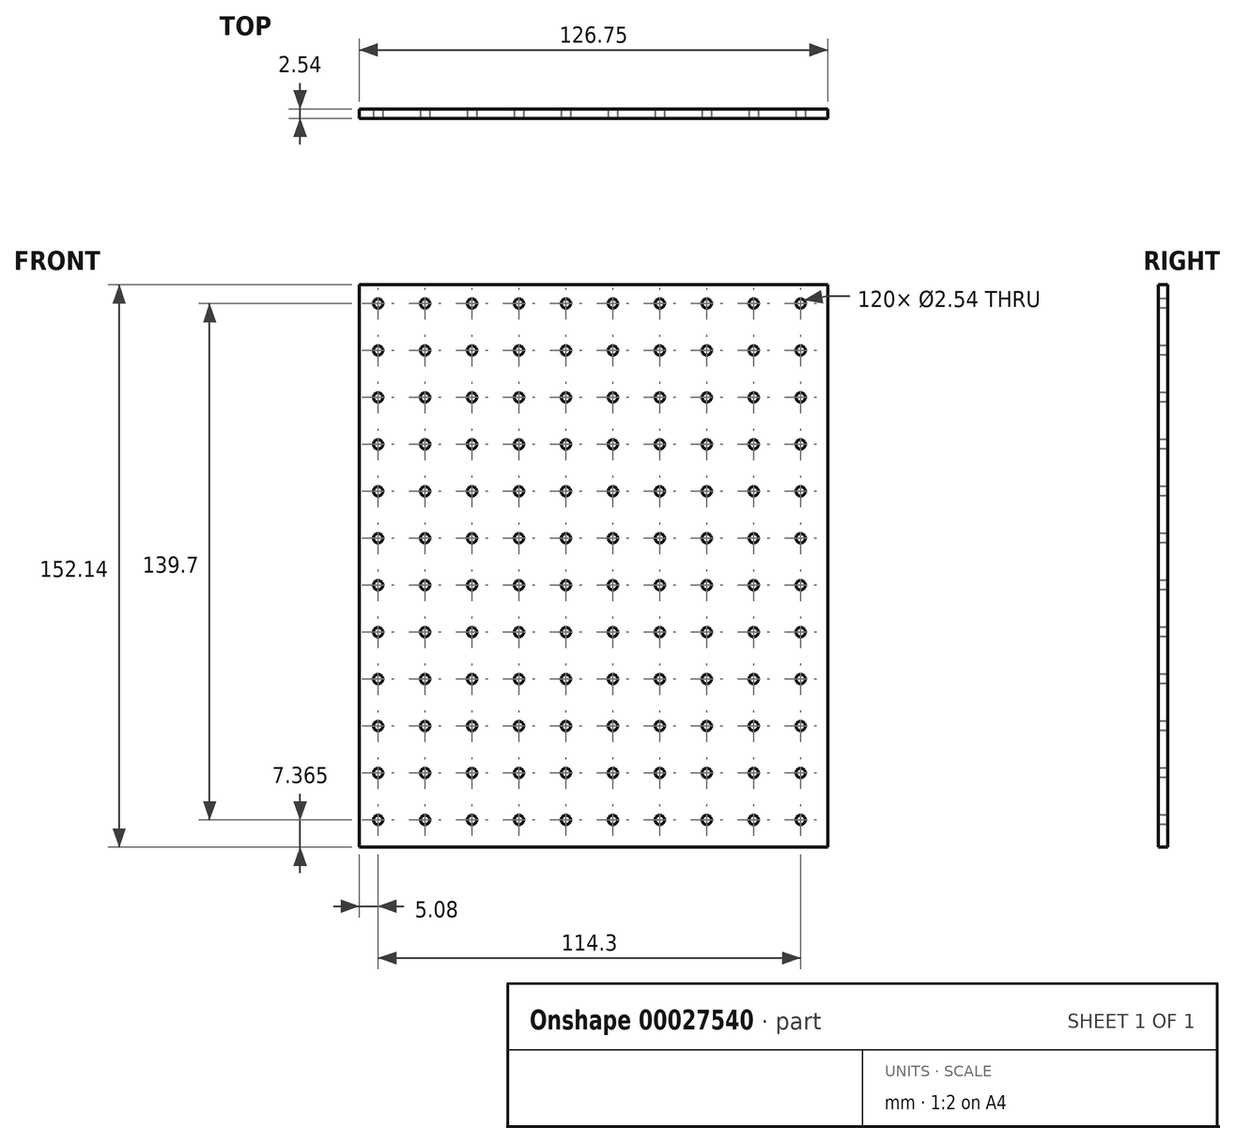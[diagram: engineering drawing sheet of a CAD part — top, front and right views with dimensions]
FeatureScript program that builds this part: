
annotation { "Feature Type Name" : "Feature", "Feature Type Description" : "" }
export const myFeature = defineFeature(function(context is Context, id is Id, definition is map)
    precondition{}
    {
        {
            var Q0;
            Q0=qCreatedBy(makeId("Front.planeOp"),FACE);
            var sketch = newSketch(context, id + "F0", { "sketchPlane" : qUnion([Q0])});
            skLineSegment(sketch, "E0.bottom", {"start": v(-42.7, 126.61) * mm, "end": v(84.04, 126.61) * mm});
            skLineSegment(sketch, "E0.top", {"start": v(-42.7, -25.53) * mm, "end": v(84.04, -25.53) * mm});
            skLineSegment(sketch, "E0.left", {"start": v(-42.7, 126.61) * mm, "end": v(-42.7, -25.53) * mm});
            skLineSegment(sketch, "E0.right", {"start": v(84.04, 126.61) * mm, "end": v(84.04, -25.53) * mm});
            skSolve(sketch);
        }
        {
            var Q0;
            Q0=makeQuery(id+"F0.imprint","IMPRINT",FACE,{"disambiguationData":[TD([[makeQuery(id+"F0.imprint","IMPRINT",EDGE,{"derivedFrom":sQuery(id+"F0.wireOp",EDGE,"E0.bottom")}),-1.0]])]});
            extrude(context, id + "F1", {"entities" : qUnion([Q0]), "depth" : 2.54 * mm});
        }
        {
            var Q0;
            Q0=makeQuery(id+"F1.opExtrude","CAP_FACE",FACE,{"disambiguationData":[OSD([sQuery(id+"F0.wireOp",EDGE,"E0.bottom"),sQuery(id+"F0.wireOp",EDGE,"E0.top"),sQuery(id+"F0.wireOp",EDGE,"E0.left"),sQuery(id+"F0.wireOp",EDGE,"E0.right")])],"isStart":false});
            var sketch = newSketch(context, id + "F2", { "sketchPlane" : qUnion([Q0])});
            skCircle(sketch, "E1", {"center": v(-37.63, 121.53) * mm, "radius": 1.27 * mm});
            skCircle(sketch, "E2.0.1.0", {"center": v(-37.63, 108.83) * mm, "radius": 1.27 * mm});
            skCircle(sketch, "E2.0.2.0", {"center": v(-37.63, 96.13) * mm, "radius": 1.27 * mm});
            skCircle(sketch, "E2.0.3.0", {"center": v(-37.63, 83.43) * mm, "radius": 1.27 * mm});
            skCircle(sketch, "E2.0.4.0", {"center": v(-37.63, 70.73) * mm, "radius": 1.27 * mm});
            skCircle(sketch, "E2.0.5.0", {"center": v(-37.63, 58.03) * mm, "radius": 1.27 * mm});
            skCircle(sketch, "E2.0.6.0", {"center": v(-37.63, 45.33) * mm, "radius": 1.27 * mm});
            skCircle(sketch, "E2.0.7.0", {"center": v(-37.63, 32.63) * mm, "radius": 1.27 * mm});
            skCircle(sketch, "E2.0.8.0", {"center": v(-37.63, 19.93) * mm, "radius": 1.27 * mm});
            skCircle(sketch, "E2.0.9.0", {"center": v(-37.63, 7.23) * mm, "radius": 1.27 * mm});
            skCircle(sketch, "E2.0.10.0", {"center": v(-37.63, -5.47) * mm, "radius": 1.27 * mm});
            skCircle(sketch, "E2.0.11.0", {"center": v(-37.63, -18.17) * mm, "radius": 1.27 * mm});
            skCircle(sketch, "E2.1.0.0", {"center": v(-24.93, 121.53) * mm, "radius": 1.27 * mm});
            skCircle(sketch, "E2.1.1.0", {"center": v(-24.93, 108.83) * mm, "radius": 1.27 * mm});
            skCircle(sketch, "E2.1.2.0", {"center": v(-24.93, 96.13) * mm, "radius": 1.27 * mm});
            skCircle(sketch, "E2.1.3.0", {"center": v(-24.93, 83.43) * mm, "radius": 1.27 * mm});
            skCircle(sketch, "E2.1.4.0", {"center": v(-24.93, 70.73) * mm, "radius": 1.27 * mm});
            skCircle(sketch, "E2.1.5.0", {"center": v(-24.93, 58.03) * mm, "radius": 1.27 * mm});
            skCircle(sketch, "E2.1.6.0", {"center": v(-24.93, 45.33) * mm, "radius": 1.27 * mm});
            skCircle(sketch, "E2.1.7.0", {"center": v(-24.93, 32.63) * mm, "radius": 1.27 * mm});
            skCircle(sketch, "E2.1.8.0", {"center": v(-24.93, 19.93) * mm, "radius": 1.27 * mm});
            skCircle(sketch, "E2.1.9.0", {"center": v(-24.93, 7.23) * mm, "radius": 1.27 * mm});
            skCircle(sketch, "E2.1.10.0", {"center": v(-24.93, -5.47) * mm, "radius": 1.27 * mm});
            skCircle(sketch, "E2.1.11.0", {"center": v(-24.93, -18.17) * mm, "radius": 1.27 * mm});
            skCircle(sketch, "E2.2.0.0", {"center": v(-12.23, 121.53) * mm, "radius": 1.27 * mm});
            skCircle(sketch, "E2.2.1.0", {"center": v(-12.23, 108.83) * mm, "radius": 1.27 * mm});
            skCircle(sketch, "E2.2.2.0", {"center": v(-12.23, 96.13) * mm, "radius": 1.27 * mm});
            skCircle(sketch, "E2.2.3.0", {"center": v(-12.23, 83.43) * mm, "radius": 1.27 * mm});
            skCircle(sketch, "E2.2.4.0", {"center": v(-12.23, 70.73) * mm, "radius": 1.27 * mm});
            skCircle(sketch, "E2.2.5.0", {"center": v(-12.23, 58.03) * mm, "radius": 1.27 * mm});
            skCircle(sketch, "E2.2.6.0", {"center": v(-12.23, 45.33) * mm, "radius": 1.27 * mm});
            skCircle(sketch, "E2.2.7.0", {"center": v(-12.23, 32.63) * mm, "radius": 1.27 * mm});
            skCircle(sketch, "E2.2.8.0", {"center": v(-12.23, 19.93) * mm, "radius": 1.27 * mm});
            skCircle(sketch, "E2.2.9.0", {"center": v(-12.23, 7.23) * mm, "radius": 1.27 * mm});
            skCircle(sketch, "E2.2.10.0", {"center": v(-12.23, -5.47) * mm, "radius": 1.27 * mm});
            skCircle(sketch, "E2.2.11.0", {"center": v(-12.23, -18.17) * mm, "radius": 1.27 * mm});
            skCircle(sketch, "E2.3.0.0", {"center": v(0.47, 121.53) * mm, "radius": 1.27 * mm});
            skCircle(sketch, "E2.3.1.0", {"center": v(0.47, 108.83) * mm, "radius": 1.27 * mm});
            skCircle(sketch, "E2.3.2.0", {"center": v(0.47, 96.13) * mm, "radius": 1.27 * mm});
            skCircle(sketch, "E2.3.3.0", {"center": v(0.47, 83.43) * mm, "radius": 1.27 * mm});
            skCircle(sketch, "E2.3.4.0", {"center": v(0.47, 70.73) * mm, "radius": 1.27 * mm});
            skCircle(sketch, "E2.3.5.0", {"center": v(0.47, 58.03) * mm, "radius": 1.27 * mm});
            skCircle(sketch, "E2.3.6.0", {"center": v(0.47, 45.33) * mm, "radius": 1.27 * mm});
            skCircle(sketch, "E2.3.7.0", {"center": v(0.47, 32.63) * mm, "radius": 1.27 * mm});
            skCircle(sketch, "E2.3.8.0", {"center": v(0.47, 19.93) * mm, "radius": 1.27 * mm});
            skCircle(sketch, "E2.3.9.0", {"center": v(0.47, 7.23) * mm, "radius": 1.27 * mm});
            skCircle(sketch, "E2.3.10.0", {"center": v(0.47, -5.47) * mm, "radius": 1.27 * mm});
            skCircle(sketch, "E2.3.11.0", {"center": v(0.47, -18.17) * mm, "radius": 1.27 * mm});
            skCircle(sketch, "E2.4.0.0", {"center": v(13.17, 121.53) * mm, "radius": 1.27 * mm});
            skCircle(sketch, "E2.4.1.0", {"center": v(13.17, 108.83) * mm, "radius": 1.27 * mm});
            skCircle(sketch, "E2.4.2.0", {"center": v(13.17, 96.13) * mm, "radius": 1.27 * mm});
            skCircle(sketch, "E2.4.3.0", {"center": v(13.17, 83.43) * mm, "radius": 1.27 * mm});
            skCircle(sketch, "E2.4.4.0", {"center": v(13.17, 70.73) * mm, "radius": 1.27 * mm});
            skCircle(sketch, "E2.4.5.0", {"center": v(13.17, 58.03) * mm, "radius": 1.27 * mm});
            skCircle(sketch, "E2.4.6.0", {"center": v(13.17, 45.33) * mm, "radius": 1.27 * mm});
            skCircle(sketch, "E2.4.7.0", {"center": v(13.17, 32.63) * mm, "radius": 1.27 * mm});
            skCircle(sketch, "E2.4.8.0", {"center": v(13.17, 19.93) * mm, "radius": 1.27 * mm});
            skCircle(sketch, "E2.4.9.0", {"center": v(13.17, 7.23) * mm, "radius": 1.27 * mm});
            skCircle(sketch, "E2.4.10.0", {"center": v(13.17, -5.47) * mm, "radius": 1.27 * mm});
            skCircle(sketch, "E2.4.11.0", {"center": v(13.17, -18.17) * mm, "radius": 1.27 * mm});
            skCircle(sketch, "E2.5.0.0", {"center": v(25.87, 121.53) * mm, "radius": 1.27 * mm});
            skCircle(sketch, "E2.5.1.0", {"center": v(25.87, 108.83) * mm, "radius": 1.27 * mm});
            skCircle(sketch, "E2.5.2.0", {"center": v(25.87, 96.13) * mm, "radius": 1.27 * mm});
            skCircle(sketch, "E2.5.3.0", {"center": v(25.87, 83.43) * mm, "radius": 1.27 * mm});
            skCircle(sketch, "E2.5.4.0", {"center": v(25.87, 70.73) * mm, "radius": 1.27 * mm});
            skCircle(sketch, "E2.5.5.0", {"center": v(25.87, 58.03) * mm, "radius": 1.27 * mm});
            skCircle(sketch, "E2.5.6.0", {"center": v(25.87, 45.33) * mm, "radius": 1.27 * mm});
            skCircle(sketch, "E2.5.7.0", {"center": v(25.87, 32.63) * mm, "radius": 1.27 * mm});
            skCircle(sketch, "E2.5.8.0", {"center": v(25.87, 19.93) * mm, "radius": 1.27 * mm});
            skCircle(sketch, "E2.5.9.0", {"center": v(25.87, 7.23) * mm, "radius": 1.27 * mm});
            skCircle(sketch, "E2.5.10.0", {"center": v(25.87, -5.47) * mm, "radius": 1.27 * mm});
            skCircle(sketch, "E2.5.11.0", {"center": v(25.87, -18.17) * mm, "radius": 1.27 * mm});
            skCircle(sketch, "E2.6.0.0", {"center": v(38.57, 121.53) * mm, "radius": 1.27 * mm});
            skCircle(sketch, "E2.6.1.0", {"center": v(38.57, 108.83) * mm, "radius": 1.27 * mm});
            skCircle(sketch, "E2.6.2.0", {"center": v(38.57, 96.13) * mm, "radius": 1.27 * mm});
            skCircle(sketch, "E2.6.3.0", {"center": v(38.57, 83.43) * mm, "radius": 1.27 * mm});
            skCircle(sketch, "E2.6.4.0", {"center": v(38.57, 70.73) * mm, "radius": 1.27 * mm});
            skCircle(sketch, "E2.6.5.0", {"center": v(38.57, 58.03) * mm, "radius": 1.27 * mm});
            skCircle(sketch, "E2.6.6.0", {"center": v(38.57, 45.33) * mm, "radius": 1.27 * mm});
            skCircle(sketch, "E2.6.7.0", {"center": v(38.57, 32.63) * mm, "radius": 1.27 * mm});
            skCircle(sketch, "E2.6.8.0", {"center": v(38.57, 19.93) * mm, "radius": 1.27 * mm});
            skCircle(sketch, "E2.6.9.0", {"center": v(38.57, 7.23) * mm, "radius": 1.27 * mm});
            skCircle(sketch, "E2.6.10.0", {"center": v(38.57, -5.47) * mm, "radius": 1.27 * mm});
            skCircle(sketch, "E2.6.11.0", {"center": v(38.57, -18.17) * mm, "radius": 1.27 * mm});
            skCircle(sketch, "E2.7.0.0", {"center": v(51.27, 121.53) * mm, "radius": 1.27 * mm});
            skCircle(sketch, "E2.7.1.0", {"center": v(51.27, 108.83) * mm, "radius": 1.27 * mm});
            skCircle(sketch, "E2.7.2.0", {"center": v(51.27, 96.13) * mm, "radius": 1.27 * mm});
            skCircle(sketch, "E2.7.3.0", {"center": v(51.27, 83.43) * mm, "radius": 1.27 * mm});
            skCircle(sketch, "E2.7.4.0", {"center": v(51.27, 70.73) * mm, "radius": 1.27 * mm});
            skCircle(sketch, "E2.7.5.0", {"center": v(51.27, 58.03) * mm, "radius": 1.27 * mm});
            skCircle(sketch, "E2.7.6.0", {"center": v(51.27, 45.33) * mm, "radius": 1.27 * mm});
            skCircle(sketch, "E2.7.7.0", {"center": v(51.27, 32.63) * mm, "radius": 1.27 * mm});
            skCircle(sketch, "E2.7.8.0", {"center": v(51.27, 19.93) * mm, "radius": 1.27 * mm});
            skCircle(sketch, "E2.7.9.0", {"center": v(51.27, 7.23) * mm, "radius": 1.27 * mm});
            skCircle(sketch, "E2.7.10.0", {"center": v(51.27, -5.47) * mm, "radius": 1.27 * mm});
            skCircle(sketch, "E2.7.11.0", {"center": v(51.27, -18.17) * mm, "radius": 1.27 * mm});
            skCircle(sketch, "E2.8.0.0", {"center": v(63.97, 121.53) * mm, "radius": 1.27 * mm});
            skCircle(sketch, "E2.8.1.0", {"center": v(63.97, 108.83) * mm, "radius": 1.27 * mm});
            skCircle(sketch, "E2.8.2.0", {"center": v(63.97, 96.13) * mm, "radius": 1.27 * mm});
            skCircle(sketch, "E2.8.3.0", {"center": v(63.97, 83.43) * mm, "radius": 1.27 * mm});
            skCircle(sketch, "E2.8.4.0", {"center": v(63.97, 70.73) * mm, "radius": 1.27 * mm});
            skCircle(sketch, "E2.8.5.0", {"center": v(63.97, 58.03) * mm, "radius": 1.27 * mm});
            skCircle(sketch, "E2.8.6.0", {"center": v(63.97, 45.33) * mm, "radius": 1.27 * mm});
            skCircle(sketch, "E2.8.7.0", {"center": v(63.97, 32.63) * mm, "radius": 1.27 * mm});
            skCircle(sketch, "E2.8.8.0", {"center": v(63.97, 19.93) * mm, "radius": 1.27 * mm});
            skCircle(sketch, "E2.8.9.0", {"center": v(63.97, 7.23) * mm, "radius": 1.27 * mm});
            skCircle(sketch, "E2.8.10.0", {"center": v(63.97, -5.47) * mm, "radius": 1.27 * mm});
            skCircle(sketch, "E2.8.11.0", {"center": v(63.97, -18.17) * mm, "radius": 1.27 * mm});
            skCircle(sketch, "E2.9.0.0", {"center": v(76.67, 121.53) * mm, "radius": 1.27 * mm});
            skCircle(sketch, "E2.9.1.0", {"center": v(76.67, 108.83) * mm, "radius": 1.27 * mm});
            skCircle(sketch, "E2.9.2.0", {"center": v(76.67, 96.13) * mm, "radius": 1.27 * mm});
            skCircle(sketch, "E2.9.3.0", {"center": v(76.67, 83.43) * mm, "radius": 1.27 * mm});
            skCircle(sketch, "E2.9.4.0", {"center": v(76.67, 70.73) * mm, "radius": 1.27 * mm});
            skCircle(sketch, "E2.9.5.0", {"center": v(76.67, 58.03) * mm, "radius": 1.27 * mm});
            skCircle(sketch, "E2.9.6.0", {"center": v(76.67, 45.33) * mm, "radius": 1.27 * mm});
            skCircle(sketch, "E2.9.7.0", {"center": v(76.67, 32.63) * mm, "radius": 1.27 * mm});
            skCircle(sketch, "E2.9.8.0", {"center": v(76.67, 19.93) * mm, "radius": 1.27 * mm});
            skCircle(sketch, "E2.9.9.0", {"center": v(76.67, 7.23) * mm, "radius": 1.27 * mm});
            skCircle(sketch, "E2.9.10.0", {"center": v(76.67, -5.47) * mm, "radius": 1.27 * mm});
            skCircle(sketch, "E2.9.11.0", {"center": v(76.67, -18.17) * mm, "radius": 1.27 * mm});
            skLineSegment(sketch, "E2.direction1", {"start": v(-37.63, 121.53) * mm, "end": v(-24.93, 121.53) * mm, "construction": true});
            skLineSegment(sketch, "E2.direction2", {"start": v(-37.63, 121.53) * mm, "end": v(-37.63, 108.83) * mm, "construction": true});
            skSolve(sketch);
        }
        {
            var Q0;
            Q0=makeQuery(id+"F2.imprint","IMPRINT",FACE,{"disambiguationData":[TD([[makeQuery(id+"F2.imprint","IMPRINT",EDGE,{"derivedFrom":sQuery(id+"F2.wireOp",EDGE,"E2.0.11.0")}),1.0]])]});
            var Q1;
            Q1=makeQuery(id+"F2.imprint","IMPRINT",FACE,{"disambiguationData":[TD([[makeQuery(id+"F2.imprint","IMPRINT",EDGE,{"derivedFrom":sQuery(id+"F2.wireOp",EDGE,"E2.1.11.0")}),1.0]])]});
            var Q2;
            Q2=makeQuery(id+"F2.imprint","IMPRINT",FACE,{"disambiguationData":[TD([[makeQuery(id+"F2.imprint","IMPRINT",EDGE,{"derivedFrom":sQuery(id+"F2.wireOp",EDGE,"E2.2.11.0")}),1.0]])]});
            var Q3;
            Q3=makeQuery(id+"F2.imprint","IMPRINT",FACE,{"disambiguationData":[TD([[makeQuery(id+"F2.imprint","IMPRINT",EDGE,{"derivedFrom":sQuery(id+"F2.wireOp",EDGE,"E2.3.11.0")}),1.0]])]});
            var Q4;
            Q4=makeQuery(id+"F2.imprint","IMPRINT",FACE,{"disambiguationData":[TD([[makeQuery(id+"F2.imprint","IMPRINT",EDGE,{"derivedFrom":sQuery(id+"F2.wireOp",EDGE,"E2.4.11.0")}),1.0]])]});
            var Q5;
            Q5=makeQuery(id+"F2.imprint","IMPRINT",FACE,{"disambiguationData":[TD([[makeQuery(id+"F2.imprint","IMPRINT",EDGE,{"derivedFrom":sQuery(id+"F2.wireOp",EDGE,"E2.5.11.0")}),1.0]])]});
            var Q6;
            Q6=makeQuery(id+"F2.imprint","IMPRINT",FACE,{"disambiguationData":[TD([[makeQuery(id+"F2.imprint","IMPRINT",EDGE,{"derivedFrom":sQuery(id+"F2.wireOp",EDGE,"E2.6.11.0")}),1.0]])]});
            var Q7;
            Q7=makeQuery(id+"F2.imprint","IMPRINT",FACE,{"disambiguationData":[TD([[makeQuery(id+"F2.imprint","IMPRINT",EDGE,{"derivedFrom":sQuery(id+"F2.wireOp",EDGE,"E2.7.11.0")}),1.0]])]});
            var Q8;
            Q8=makeQuery(id+"F2.imprint","IMPRINT",FACE,{"disambiguationData":[TD([[makeQuery(id+"F2.imprint","IMPRINT",EDGE,{"derivedFrom":sQuery(id+"F2.wireOp",EDGE,"E2.8.11.0")}),1.0]])]});
            var Q9;
            Q9=makeQuery(id+"F2.imprint","IMPRINT",FACE,{"disambiguationData":[TD([[makeQuery(id+"F2.imprint","IMPRINT",EDGE,{"derivedFrom":sQuery(id+"F2.wireOp",EDGE,"E2.9.11.0")}),1.0]])]});
            var Q10;
            Q10=makeQuery(id+"F2.imprint","IMPRINT",FACE,{"disambiguationData":[TD([[makeQuery(id+"F2.imprint","IMPRINT",EDGE,{"derivedFrom":sQuery(id+"F2.wireOp",EDGE,"E2.9.10.0")}),1.0]])]});
            var Q11;
            Q11=makeQuery(id+"F2.imprint","IMPRINT",FACE,{"disambiguationData":[TD([[makeQuery(id+"F2.imprint","IMPRINT",EDGE,{"derivedFrom":sQuery(id+"F2.wireOp",EDGE,"E2.9.9.0")}),1.0]])]});
            var Q12;
            Q12=makeQuery(id+"F2.imprint","IMPRINT",FACE,{"disambiguationData":[TD([[makeQuery(id+"F2.imprint","IMPRINT",EDGE,{"derivedFrom":sQuery(id+"F2.wireOp",EDGE,"E2.8.10.0")}),1.0]])]});
            var Q13;
            Q13=makeQuery(id+"F2.imprint","IMPRINT",FACE,{"disambiguationData":[TD([[makeQuery(id+"F2.imprint","IMPRINT",EDGE,{"derivedFrom":sQuery(id+"F2.wireOp",EDGE,"E2.8.9.0")}),1.0]])]});
            var Q14;
            Q14=makeQuery(id+"F2.imprint","IMPRINT",FACE,{"disambiguationData":[TD([[makeQuery(id+"F2.imprint","IMPRINT",EDGE,{"derivedFrom":sQuery(id+"F2.wireOp",EDGE,"E2.7.9.0")}),1.0]])]});
            var Q15;
            Q15=makeQuery(id+"F2.imprint","IMPRINT",FACE,{"disambiguationData":[TD([[makeQuery(id+"F2.imprint","IMPRINT",EDGE,{"derivedFrom":sQuery(id+"F2.wireOp",EDGE,"E2.7.10.0")}),1.0]])]});
            var Q16;
            Q16=makeQuery(id+"F2.imprint","IMPRINT",FACE,{"disambiguationData":[TD([[makeQuery(id+"F2.imprint","IMPRINT",EDGE,{"derivedFrom":sQuery(id+"F2.wireOp",EDGE,"E2.6.10.0")}),1.0]])]});
            var Q17;
            Q17=makeQuery(id+"F2.imprint","IMPRINT",FACE,{"disambiguationData":[TD([[makeQuery(id+"F2.imprint","IMPRINT",EDGE,{"derivedFrom":sQuery(id+"F2.wireOp",EDGE,"E2.6.9.0")}),1.0]])]});
            var Q18;
            Q18=makeQuery(id+"F2.imprint","IMPRINT",FACE,{"disambiguationData":[TD([[makeQuery(id+"F2.imprint","IMPRINT",EDGE,{"derivedFrom":sQuery(id+"F2.wireOp",EDGE,"E2.4.9.0")}),1.0]])]});
            var Q19;
            Q19=makeQuery(id+"F2.imprint","IMPRINT",FACE,{"disambiguationData":[TD([[makeQuery(id+"F2.imprint","IMPRINT",EDGE,{"derivedFrom":sQuery(id+"F2.wireOp",EDGE,"E2.3.9.0")}),1.0]])]});
            var Q20;
            Q20=makeQuery(id+"F2.imprint","IMPRINT",FACE,{"disambiguationData":[TD([[makeQuery(id+"F2.imprint","IMPRINT",EDGE,{"derivedFrom":sQuery(id+"F2.wireOp",EDGE,"E2.3.10.0")}),1.0]])]});
            var Q21;
            Q21=makeQuery(id+"F2.imprint","IMPRINT",FACE,{"disambiguationData":[TD([[makeQuery(id+"F2.imprint","IMPRINT",EDGE,{"derivedFrom":sQuery(id+"F2.wireOp",EDGE,"E2.2.10.0")}),1.0]])]});
            var Q22;
            Q22=makeQuery(id+"F2.imprint","IMPRINT",FACE,{"disambiguationData":[TD([[makeQuery(id+"F2.imprint","IMPRINT",EDGE,{"derivedFrom":sQuery(id+"F2.wireOp",EDGE,"E2.5.9.0")}),1.0]])]});
            var Q23;
            Q23=makeQuery(id+"F2.imprint","IMPRINT",FACE,{"disambiguationData":[TD([[makeQuery(id+"F2.imprint","IMPRINT",EDGE,{"derivedFrom":sQuery(id+"F2.wireOp",EDGE,"E2.5.10.0")}),1.0]])]});
            var Q24;
            Q24=makeQuery(id+"F2.imprint","IMPRINT",FACE,{"disambiguationData":[TD([[makeQuery(id+"F2.imprint","IMPRINT",EDGE,{"derivedFrom":sQuery(id+"F2.wireOp",EDGE,"E2.4.10.0")}),1.0]])]});
            var Q25;
            Q25=makeQuery(id+"F2.imprint","IMPRINT",FACE,{"disambiguationData":[TD([[makeQuery(id+"F2.imprint","IMPRINT",EDGE,{"derivedFrom":sQuery(id+"F2.wireOp",EDGE,"E2.1.10.0")}),1.0]])]});
            var Q26;
            Q26=makeQuery(id+"F2.imprint","IMPRINT",FACE,{"disambiguationData":[TD([[makeQuery(id+"F2.imprint","IMPRINT",EDGE,{"derivedFrom":sQuery(id+"F2.wireOp",EDGE,"E2.0.10.0")}),1.0]])]});
            var Q27;
            Q27=makeQuery(id+"F2.imprint","IMPRINT",FACE,{"disambiguationData":[TD([[makeQuery(id+"F2.imprint","IMPRINT",EDGE,{"derivedFrom":sQuery(id+"F2.wireOp",EDGE,"E2.0.9.0")}),1.0]])]});
            var Q28;
            Q28=makeQuery(id+"F2.imprint","IMPRINT",FACE,{"disambiguationData":[TD([[makeQuery(id+"F2.imprint","IMPRINT",EDGE,{"derivedFrom":sQuery(id+"F2.wireOp",EDGE,"E2.1.9.0")}),1.0]])]});
            var Q29;
            Q29=makeQuery(id+"F2.imprint","IMPRINT",FACE,{"disambiguationData":[TD([[makeQuery(id+"F2.imprint","IMPRINT",EDGE,{"derivedFrom":sQuery(id+"F2.wireOp",EDGE,"E2.2.9.0")}),1.0]])]});
            var Q30;
            Q30=makeQuery(id+"F2.imprint","IMPRINT",FACE,{"disambiguationData":[TD([[makeQuery(id+"F2.imprint","IMPRINT",EDGE,{"derivedFrom":sQuery(id+"F2.wireOp",EDGE,"E2.0.8.0")}),1.0]])]});
            var Q31;
            Q31=makeQuery(id+"F2.imprint","IMPRINT",FACE,{"disambiguationData":[TD([[makeQuery(id+"F2.imprint","IMPRINT",EDGE,{"derivedFrom":sQuery(id+"F2.wireOp",EDGE,"E2.1.8.0")}),1.0]])]});
            var Q32;
            Q32=makeQuery(id+"F2.imprint","IMPRINT",FACE,{"disambiguationData":[TD([[makeQuery(id+"F2.imprint","IMPRINT",EDGE,{"derivedFrom":sQuery(id+"F2.wireOp",EDGE,"E2.2.8.0")}),1.0]])]});
            var Q33;
            Q33=makeQuery(id+"F2.imprint","IMPRINT",FACE,{"disambiguationData":[TD([[makeQuery(id+"F2.imprint","IMPRINT",EDGE,{"derivedFrom":sQuery(id+"F2.wireOp",EDGE,"E2.3.8.0")}),1.0]])]});
            var Q34;
            Q34=makeQuery(id+"F2.imprint","IMPRINT",FACE,{"disambiguationData":[TD([[makeQuery(id+"F2.imprint","IMPRINT",EDGE,{"derivedFrom":sQuery(id+"F2.wireOp",EDGE,"E2.4.8.0")}),1.0]])]});
            var Q35;
            Q35=makeQuery(id+"F2.imprint","IMPRINT",FACE,{"disambiguationData":[TD([[makeQuery(id+"F2.imprint","IMPRINT",EDGE,{"derivedFrom":sQuery(id+"F2.wireOp",EDGE,"E2.5.8.0")}),1.0]])]});
            var Q36;
            Q36=makeQuery(id+"F2.imprint","IMPRINT",FACE,{"disambiguationData":[TD([[makeQuery(id+"F2.imprint","IMPRINT",EDGE,{"derivedFrom":sQuery(id+"F2.wireOp",EDGE,"E2.6.8.0")}),1.0]])]});
            var Q37;
            Q37=makeQuery(id+"F2.imprint","IMPRINT",FACE,{"disambiguationData":[TD([[makeQuery(id+"F2.imprint","IMPRINT",EDGE,{"derivedFrom":sQuery(id+"F2.wireOp",EDGE,"E2.7.8.0")}),1.0]])]});
            var Q38;
            Q38=makeQuery(id+"F2.imprint","IMPRINT",FACE,{"disambiguationData":[TD([[makeQuery(id+"F2.imprint","IMPRINT",EDGE,{"derivedFrom":sQuery(id+"F2.wireOp",EDGE,"E2.8.8.0")}),1.0]])]});
            var Q39;
            Q39=makeQuery(id+"F2.imprint","IMPRINT",FACE,{"disambiguationData":[TD([[makeQuery(id+"F2.imprint","IMPRINT",EDGE,{"derivedFrom":sQuery(id+"F2.wireOp",EDGE,"E2.9.8.0")}),1.0]])]});
            var Q40;
            Q40=makeQuery(id+"F2.imprint","IMPRINT",FACE,{"disambiguationData":[TD([[makeQuery(id+"F2.imprint","IMPRINT",EDGE,{"derivedFrom":sQuery(id+"F2.wireOp",EDGE,"E2.9.7.0")}),1.0]])]});
            var Q41;
            Q41=makeQuery(id+"F2.imprint","IMPRINT",FACE,{"disambiguationData":[TD([[makeQuery(id+"F2.imprint","IMPRINT",EDGE,{"derivedFrom":sQuery(id+"F2.wireOp",EDGE,"E2.9.6.0")}),1.0]])]});
            var Q42;
            Q42=makeQuery(id+"F2.imprint","IMPRINT",FACE,{"disambiguationData":[TD([[makeQuery(id+"F2.imprint","IMPRINT",EDGE,{"derivedFrom":sQuery(id+"F2.wireOp",EDGE,"E2.8.6.0")}),1.0]])]});
            var Q43;
            Q43=makeQuery(id+"F2.imprint","IMPRINT",FACE,{"disambiguationData":[TD([[makeQuery(id+"F2.imprint","IMPRINT",EDGE,{"derivedFrom":sQuery(id+"F2.wireOp",EDGE,"E2.8.7.0")}),1.0]])]});
            var Q44;
            Q44=makeQuery(id+"F2.imprint","IMPRINT",FACE,{"disambiguationData":[TD([[makeQuery(id+"F2.imprint","IMPRINT",EDGE,{"derivedFrom":sQuery(id+"F2.wireOp",EDGE,"E2.7.7.0")}),1.0]])]});
            var Q45;
            Q45=makeQuery(id+"F2.imprint","IMPRINT",FACE,{"disambiguationData":[TD([[makeQuery(id+"F2.imprint","IMPRINT",EDGE,{"derivedFrom":sQuery(id+"F2.wireOp",EDGE,"E2.7.6.0")}),1.0]])]});
            var Q46;
            Q46=makeQuery(id+"F2.imprint","IMPRINT",FACE,{"disambiguationData":[TD([[makeQuery(id+"F2.imprint","IMPRINT",EDGE,{"derivedFrom":sQuery(id+"F2.wireOp",EDGE,"E2.6.6.0")}),1.0]])]});
            var Q47;
            Q47=makeQuery(id+"F2.imprint","IMPRINT",FACE,{"disambiguationData":[TD([[makeQuery(id+"F2.imprint","IMPRINT",EDGE,{"derivedFrom":sQuery(id+"F2.wireOp",EDGE,"E2.6.7.0")}),1.0]])]});
            var Q48;
            Q48=makeQuery(id+"F2.imprint","IMPRINT",FACE,{"disambiguationData":[TD([[makeQuery(id+"F2.imprint","IMPRINT",EDGE,{"derivedFrom":sQuery(id+"F2.wireOp",EDGE,"E2.5.7.0")}),1.0]])]});
            var Q49;
            Q49=makeQuery(id+"F2.imprint","IMPRINT",FACE,{"disambiguationData":[TD([[makeQuery(id+"F2.imprint","IMPRINT",EDGE,{"derivedFrom":sQuery(id+"F2.wireOp",EDGE,"E2.5.6.0")}),1.0]])]});
            var Q50;
            Q50=makeQuery(id+"F2.imprint","IMPRINT",FACE,{"disambiguationData":[TD([[makeQuery(id+"F2.imprint","IMPRINT",EDGE,{"derivedFrom":sQuery(id+"F2.wireOp",EDGE,"E2.4.6.0")}),1.0]])]});
            var Q51;
            Q51=makeQuery(id+"F2.imprint","IMPRINT",FACE,{"disambiguationData":[TD([[makeQuery(id+"F2.imprint","IMPRINT",EDGE,{"derivedFrom":sQuery(id+"F2.wireOp",EDGE,"E2.4.7.0")}),1.0]])]});
            var Q52;
            Q52=makeQuery(id+"F2.imprint","IMPRINT",FACE,{"disambiguationData":[TD([[makeQuery(id+"F2.imprint","IMPRINT",EDGE,{"derivedFrom":sQuery(id+"F2.wireOp",EDGE,"E2.3.7.0")}),1.0]])]});
            var Q53;
            Q53=makeQuery(id+"F2.imprint","IMPRINT",FACE,{"disambiguationData":[TD([[makeQuery(id+"F2.imprint","IMPRINT",EDGE,{"derivedFrom":sQuery(id+"F2.wireOp",EDGE,"E2.3.6.0")}),1.0]])]});
            var Q54;
            Q54=makeQuery(id+"F2.imprint","IMPRINT",FACE,{"disambiguationData":[TD([[makeQuery(id+"F2.imprint","IMPRINT",EDGE,{"derivedFrom":sQuery(id+"F2.wireOp",EDGE,"E2.2.6.0")}),1.0]])]});
            var Q55;
            Q55=makeQuery(id+"F2.imprint","IMPRINT",FACE,{"disambiguationData":[TD([[makeQuery(id+"F2.imprint","IMPRINT",EDGE,{"derivedFrom":sQuery(id+"F2.wireOp",EDGE,"E2.2.7.0")}),1.0]])]});
            var Q56;
            Q56=makeQuery(id+"F2.imprint","IMPRINT",FACE,{"disambiguationData":[TD([[makeQuery(id+"F2.imprint","IMPRINT",EDGE,{"derivedFrom":sQuery(id+"F2.wireOp",EDGE,"E2.1.7.0")}),1.0]])]});
            var Q57;
            Q57=makeQuery(id+"F2.imprint","IMPRINT",FACE,{"disambiguationData":[TD([[makeQuery(id+"F2.imprint","IMPRINT",EDGE,{"derivedFrom":sQuery(id+"F2.wireOp",EDGE,"E2.1.6.0")}),1.0]])]});
            var Q58;
            Q58=makeQuery(id+"F2.imprint","IMPRINT",FACE,{"disambiguationData":[TD([[makeQuery(id+"F2.imprint","IMPRINT",EDGE,{"derivedFrom":sQuery(id+"F2.wireOp",EDGE,"E2.0.6.0")}),1.0]])]});
            var Q59;
            Q59=makeQuery(id+"F2.imprint","IMPRINT",FACE,{"disambiguationData":[TD([[makeQuery(id+"F2.imprint","IMPRINT",EDGE,{"derivedFrom":sQuery(id+"F2.wireOp",EDGE,"E2.0.7.0")}),1.0]])]});
            var Q60;
            Q60=makeQuery(id+"F2.imprint","IMPRINT",FACE,{"disambiguationData":[TD([[makeQuery(id+"F2.imprint","IMPRINT",EDGE,{"derivedFrom":sQuery(id+"F2.wireOp",EDGE,"E2.0.5.0")}),1.0]])]});
            var Q61;
            Q61=makeQuery(id+"F2.imprint","IMPRINT",FACE,{"disambiguationData":[TD([[makeQuery(id+"F2.imprint","IMPRINT",EDGE,{"derivedFrom":sQuery(id+"F2.wireOp",EDGE,"E2.0.4.0")}),1.0]])]});
            var Q62;
            Q62=makeQuery(id+"F2.imprint","IMPRINT",FACE,{"disambiguationData":[TD([[makeQuery(id+"F2.imprint","IMPRINT",EDGE,{"derivedFrom":sQuery(id+"F2.wireOp",EDGE,"E2.0.3.0")}),1.0]])]});
            var Q63;
            Q63=makeQuery(id+"F2.imprint","IMPRINT",FACE,{"disambiguationData":[TD([[makeQuery(id+"F2.imprint","IMPRINT",EDGE,{"derivedFrom":sQuery(id+"F2.wireOp",EDGE,"E2.0.2.0")}),1.0]])]});
            var Q64;
            Q64=makeQuery(id+"F2.imprint","IMPRINT",FACE,{"disambiguationData":[TD([[makeQuery(id+"F2.imprint","IMPRINT",EDGE,{"derivedFrom":sQuery(id+"F2.wireOp",EDGE,"E2.1.2.0")}),1.0]])]});
            var Q65;
            Q65=makeQuery(id+"F2.imprint","IMPRINT",FACE,{"disambiguationData":[TD([[makeQuery(id+"F2.imprint","IMPRINT",EDGE,{"derivedFrom":sQuery(id+"F2.wireOp",EDGE,"E2.1.3.0")}),1.0]])]});
            var Q66;
            Q66=makeQuery(id+"F2.imprint","IMPRINT",FACE,{"disambiguationData":[TD([[makeQuery(id+"F2.imprint","IMPRINT",EDGE,{"derivedFrom":sQuery(id+"F2.wireOp",EDGE,"E2.1.4.0")}),1.0]])]});
            var Q67;
            Q67=makeQuery(id+"F2.imprint","IMPRINT",FACE,{"disambiguationData":[TD([[makeQuery(id+"F2.imprint","IMPRINT",EDGE,{"derivedFrom":sQuery(id+"F2.wireOp",EDGE,"E2.1.5.0")}),1.0]])]});
            var Q68;
            Q68=makeQuery(id+"F2.imprint","IMPRINT",FACE,{"disambiguationData":[TD([[makeQuery(id+"F2.imprint","IMPRINT",EDGE,{"derivedFrom":sQuery(id+"F2.wireOp",EDGE,"E2.2.5.0")}),1.0]])]});
            var Q69;
            Q69=makeQuery(id+"F2.imprint","IMPRINT",FACE,{"disambiguationData":[TD([[makeQuery(id+"F2.imprint","IMPRINT",EDGE,{"derivedFrom":sQuery(id+"F2.wireOp",EDGE,"E2.2.4.0")}),1.0]])]});
            var Q70;
            Q70=makeQuery(id+"F2.imprint","IMPRINT",FACE,{"disambiguationData":[TD([[makeQuery(id+"F2.imprint","IMPRINT",EDGE,{"derivedFrom":sQuery(id+"F2.wireOp",EDGE,"E2.2.3.0")}),1.0]])]});
            var Q71;
            Q71=makeQuery(id+"F2.imprint","IMPRINT",FACE,{"disambiguationData":[TD([[makeQuery(id+"F2.imprint","IMPRINT",EDGE,{"derivedFrom":sQuery(id+"F2.wireOp",EDGE,"E2.2.2.0")}),1.0]])]});
            var Q72;
            Q72=makeQuery(id+"F2.imprint","IMPRINT",FACE,{"disambiguationData":[TD([[makeQuery(id+"F2.imprint","IMPRINT",EDGE,{"derivedFrom":sQuery(id+"F2.wireOp",EDGE,"E2.3.2.0")}),1.0]])]});
            var Q73;
            Q73=makeQuery(id+"F2.imprint","IMPRINT",FACE,{"disambiguationData":[TD([[makeQuery(id+"F2.imprint","IMPRINT",EDGE,{"derivedFrom":sQuery(id+"F2.wireOp",EDGE,"E2.4.2.0")}),1.0]])]});
            var Q74;
            Q74=makeQuery(id+"F2.imprint","IMPRINT",FACE,{"disambiguationData":[TD([[makeQuery(id+"F2.imprint","IMPRINT",EDGE,{"derivedFrom":sQuery(id+"F2.wireOp",EDGE,"E2.5.2.0")}),1.0]])]});
            var Q75;
            Q75=makeQuery(id+"F2.imprint","IMPRINT",FACE,{"disambiguationData":[TD([[makeQuery(id+"F2.imprint","IMPRINT",EDGE,{"derivedFrom":sQuery(id+"F2.wireOp",EDGE,"E2.5.3.0")}),1.0]])]});
            var Q76;
            Q76=makeQuery(id+"F2.imprint","IMPRINT",FACE,{"disambiguationData":[TD([[makeQuery(id+"F2.imprint","IMPRINT",EDGE,{"derivedFrom":sQuery(id+"F2.wireOp",EDGE,"E2.4.3.0")}),1.0]])]});
            var Q77;
            Q77=makeQuery(id+"F2.imprint","IMPRINT",FACE,{"disambiguationData":[TD([[makeQuery(id+"F2.imprint","IMPRINT",EDGE,{"derivedFrom":sQuery(id+"F2.wireOp",EDGE,"E2.3.3.0")}),1.0]])]});
            var Q78;
            Q78=makeQuery(id+"F2.imprint","IMPRINT",FACE,{"disambiguationData":[TD([[makeQuery(id+"F2.imprint","IMPRINT",EDGE,{"derivedFrom":sQuery(id+"F2.wireOp",EDGE,"E2.3.4.0")}),1.0]])]});
            var Q79;
            Q79=makeQuery(id+"F2.imprint","IMPRINT",FACE,{"disambiguationData":[TD([[makeQuery(id+"F2.imprint","IMPRINT",EDGE,{"derivedFrom":sQuery(id+"F2.wireOp",EDGE,"E2.4.4.0")}),1.0]])]});
            var Q80;
            Q80=makeQuery(id+"F2.imprint","IMPRINT",FACE,{"disambiguationData":[TD([[makeQuery(id+"F2.imprint","IMPRINT",EDGE,{"derivedFrom":sQuery(id+"F2.wireOp",EDGE,"E2.5.4.0")}),1.0]])]});
            var Q81;
            Q81=makeQuery(id+"F2.imprint","IMPRINT",FACE,{"disambiguationData":[TD([[makeQuery(id+"F2.imprint","IMPRINT",EDGE,{"derivedFrom":sQuery(id+"F2.wireOp",EDGE,"E2.5.5.0")}),1.0]])]});
            var Q82;
            Q82=makeQuery(id+"F2.imprint","IMPRINT",FACE,{"disambiguationData":[TD([[makeQuery(id+"F2.imprint","IMPRINT",EDGE,{"derivedFrom":sQuery(id+"F2.wireOp",EDGE,"E2.4.5.0")}),1.0]])]});
            var Q83;
            Q83=makeQuery(id+"F2.imprint","IMPRINT",FACE,{"disambiguationData":[TD([[makeQuery(id+"F2.imprint","IMPRINT",EDGE,{"derivedFrom":sQuery(id+"F2.wireOp",EDGE,"E2.3.5.0")}),1.0]])]});
            var Q84;
            Q84=makeQuery(id+"F2.imprint","IMPRINT",FACE,{"disambiguationData":[TD([[makeQuery(id+"F2.imprint","IMPRINT",EDGE,{"derivedFrom":sQuery(id+"F2.wireOp",EDGE,"E2.6.5.0")}),1.0]])]});
            var Q85;
            Q85=makeQuery(id+"F2.imprint","IMPRINT",FACE,{"disambiguationData":[TD([[makeQuery(id+"F2.imprint","IMPRINT",EDGE,{"derivedFrom":sQuery(id+"F2.wireOp",EDGE,"E2.7.5.0")}),1.0]])]});
            var Q86;
            Q86=makeQuery(id+"F2.imprint","IMPRINT",FACE,{"disambiguationData":[TD([[makeQuery(id+"F2.imprint","IMPRINT",EDGE,{"derivedFrom":sQuery(id+"F2.wireOp",EDGE,"E2.8.5.0")}),1.0]])]});
            var Q87;
            Q87=makeQuery(id+"F2.imprint","IMPRINT",FACE,{"disambiguationData":[TD([[makeQuery(id+"F2.imprint","IMPRINT",EDGE,{"derivedFrom":sQuery(id+"F2.wireOp",EDGE,"E2.9.5.0")}),1.0]])]});
            var Q88;
            Q88=makeQuery(id+"F2.imprint","IMPRINT",FACE,{"disambiguationData":[TD([[makeQuery(id+"F2.imprint","IMPRINT",EDGE,{"derivedFrom":sQuery(id+"F2.wireOp",EDGE,"E2.9.4.0")}),1.0]])]});
            var Q89;
            Q89=makeQuery(id+"F2.imprint","IMPRINT",FACE,{"disambiguationData":[TD([[makeQuery(id+"F2.imprint","IMPRINT",EDGE,{"derivedFrom":sQuery(id+"F2.wireOp",EDGE,"E2.8.4.0")}),1.0]])]});
            var Q90;
            Q90=makeQuery(id+"F2.imprint","IMPRINT",FACE,{"disambiguationData":[TD([[makeQuery(id+"F2.imprint","IMPRINT",EDGE,{"derivedFrom":sQuery(id+"F2.wireOp",EDGE,"E2.7.4.0")}),1.0]])]});
            var Q91;
            Q91=makeQuery(id+"F2.imprint","IMPRINT",FACE,{"disambiguationData":[TD([[makeQuery(id+"F2.imprint","IMPRINT",EDGE,{"derivedFrom":sQuery(id+"F2.wireOp",EDGE,"E2.6.4.0")}),1.0]])]});
            var Q92;
            Q92=makeQuery(id+"F2.imprint","IMPRINT",FACE,{"disambiguationData":[TD([[makeQuery(id+"F2.imprint","IMPRINT",EDGE,{"derivedFrom":sQuery(id+"F2.wireOp",EDGE,"E2.6.3.0")}),1.0]])]});
            var Q93;
            Q93=makeQuery(id+"F2.imprint","IMPRINT",FACE,{"disambiguationData":[TD([[makeQuery(id+"F2.imprint","IMPRINT",EDGE,{"derivedFrom":sQuery(id+"F2.wireOp",EDGE,"E2.6.2.0")}),1.0]])]});
            var Q94;
            Q94=makeQuery(id+"F2.imprint","IMPRINT",FACE,{"disambiguationData":[TD([[makeQuery(id+"F2.imprint","IMPRINT",EDGE,{"derivedFrom":sQuery(id+"F2.wireOp",EDGE,"E2.7.2.0")}),1.0]])]});
            var Q95;
            Q95=makeQuery(id+"F2.imprint","IMPRINT",FACE,{"disambiguationData":[TD([[makeQuery(id+"F2.imprint","IMPRINT",EDGE,{"derivedFrom":sQuery(id+"F2.wireOp",EDGE,"E2.7.3.0")}),1.0]])]});
            var Q96;
            Q96=makeQuery(id+"F2.imprint","IMPRINT",FACE,{"disambiguationData":[TD([[makeQuery(id+"F2.imprint","IMPRINT",EDGE,{"derivedFrom":sQuery(id+"F2.wireOp",EDGE,"E2.8.3.0")}),1.0]])]});
            var Q97;
            Q97=makeQuery(id+"F2.imprint","IMPRINT",FACE,{"disambiguationData":[TD([[makeQuery(id+"F2.imprint","IMPRINT",EDGE,{"derivedFrom":sQuery(id+"F2.wireOp",EDGE,"E2.8.2.0")}),1.0]])]});
            var Q98;
            Q98=makeQuery(id+"F2.imprint","IMPRINT",FACE,{"disambiguationData":[TD([[makeQuery(id+"F2.imprint","IMPRINT",EDGE,{"derivedFrom":sQuery(id+"F2.wireOp",EDGE,"E2.9.2.0")}),1.0]])]});
            var Q99;
            Q99=makeQuery(id+"F2.imprint","IMPRINT",FACE,{"disambiguationData":[TD([[makeQuery(id+"F2.imprint","IMPRINT",EDGE,{"derivedFrom":sQuery(id+"F2.wireOp",EDGE,"E2.9.3.0")}),1.0]])]});
            var Q100;
            Q100=makeQuery(id+"F2.imprint","IMPRINT",FACE,{"disambiguationData":[TD([[makeQuery(id+"F2.imprint","IMPRINT",EDGE,{"derivedFrom":sQuery(id+"F2.wireOp",EDGE,"E2.9.1.0")}),1.0]])]});
            var Q101;
            Q101=makeQuery(id+"F2.imprint","IMPRINT",FACE,{"disambiguationData":[TD([[makeQuery(id+"F2.imprint","IMPRINT",EDGE,{"derivedFrom":sQuery(id+"F2.wireOp",EDGE,"E2.9.0.0")}),1.0]])]});
            var Q102;
            Q102=makeQuery(id+"F2.imprint","IMPRINT",FACE,{"disambiguationData":[TD([[makeQuery(id+"F2.imprint","IMPRINT",EDGE,{"derivedFrom":sQuery(id+"F2.wireOp",EDGE,"E2.8.0.0")}),1.0]])]});
            var Q103;
            Q103=makeQuery(id+"F2.imprint","IMPRINT",FACE,{"disambiguationData":[TD([[makeQuery(id+"F2.imprint","IMPRINT",EDGE,{"derivedFrom":sQuery(id+"F2.wireOp",EDGE,"E2.7.0.0")}),1.0]])]});
            var Q104;
            Q104=makeQuery(id+"F2.imprint","IMPRINT",FACE,{"disambiguationData":[TD([[makeQuery(id+"F2.imprint","IMPRINT",EDGE,{"derivedFrom":sQuery(id+"F2.wireOp",EDGE,"E2.7.1.0")}),1.0]])]});
            var Q105;
            Q105=makeQuery(id+"F2.imprint","IMPRINT",FACE,{"disambiguationData":[TD([[makeQuery(id+"F2.imprint","IMPRINT",EDGE,{"derivedFrom":sQuery(id+"F2.wireOp",EDGE,"E2.8.1.0")}),1.0]])]});
            var Q106;
            Q106=makeQuery(id+"F2.imprint","IMPRINT",FACE,{"disambiguationData":[TD([[makeQuery(id+"F2.imprint","IMPRINT",EDGE,{"derivedFrom":sQuery(id+"F2.wireOp",EDGE,"E2.6.1.0")}),1.0]])]});
            var Q107;
            Q107=makeQuery(id+"F2.imprint","IMPRINT",FACE,{"disambiguationData":[TD([[makeQuery(id+"F2.imprint","IMPRINT",EDGE,{"derivedFrom":sQuery(id+"F2.wireOp",EDGE,"E2.6.0.0")}),1.0]])]});
            var Q108;
            Q108=makeQuery(id+"F2.imprint","IMPRINT",FACE,{"disambiguationData":[TD([[makeQuery(id+"F2.imprint","IMPRINT",EDGE,{"derivedFrom":sQuery(id+"F2.wireOp",EDGE,"E2.5.0.0")}),1.0]])]});
            var Q109;
            Q109=makeQuery(id+"F2.imprint","IMPRINT",FACE,{"disambiguationData":[TD([[makeQuery(id+"F2.imprint","IMPRINT",EDGE,{"derivedFrom":sQuery(id+"F2.wireOp",EDGE,"E2.5.1.0")}),1.0]])]});
            var Q110;
            Q110=makeQuery(id+"F2.imprint","IMPRINT",FACE,{"disambiguationData":[TD([[makeQuery(id+"F2.imprint","IMPRINT",EDGE,{"derivedFrom":sQuery(id+"F2.wireOp",EDGE,"E2.4.1.0")}),1.0]])]});
            var Q111;
            Q111=makeQuery(id+"F2.imprint","IMPRINT",FACE,{"disambiguationData":[TD([[makeQuery(id+"F2.imprint","IMPRINT",EDGE,{"derivedFrom":sQuery(id+"F2.wireOp",EDGE,"E2.4.0.0")}),1.0]])]});
            var Q112;
            Q112=makeQuery(id+"F2.imprint","IMPRINT",FACE,{"disambiguationData":[TD([[makeQuery(id+"F2.imprint","IMPRINT",EDGE,{"derivedFrom":sQuery(id+"F2.wireOp",EDGE,"E2.3.0.0")}),1.0]])]});
            var Q113;
            Q113=makeQuery(id+"F2.imprint","IMPRINT",FACE,{"disambiguationData":[TD([[makeQuery(id+"F2.imprint","IMPRINT",EDGE,{"derivedFrom":sQuery(id+"F2.wireOp",EDGE,"E2.3.1.0")}),1.0]])]});
            var Q114;
            Q114=makeQuery(id+"F2.imprint","IMPRINT",FACE,{"disambiguationData":[TD([[makeQuery(id+"F2.imprint","IMPRINT",EDGE,{"derivedFrom":sQuery(id+"F2.wireOp",EDGE,"E2.2.1.0")}),1.0]])]});
            var Q115;
            Q115=makeQuery(id+"F2.imprint","IMPRINT",FACE,{"disambiguationData":[TD([[makeQuery(id+"F2.imprint","IMPRINT",EDGE,{"derivedFrom":sQuery(id+"F2.wireOp",EDGE,"E2.2.0.0")}),1.0]])]});
            var Q116;
            Q116=makeQuery(id+"F2.imprint","IMPRINT",FACE,{"disambiguationData":[TD([[makeQuery(id+"F2.imprint","IMPRINT",EDGE,{"derivedFrom":sQuery(id+"F2.wireOp",EDGE,"E2.1.0.0")}),1.0]])]});
            var Q117;
            Q117=makeQuery(id+"F2.imprint","IMPRINT",FACE,{"disambiguationData":[TD([[makeQuery(id+"F2.imprint","IMPRINT",EDGE,{"derivedFrom":sQuery(id+"F2.wireOp",EDGE,"E2.1.1.0")}),1.0]])]});
            var Q118;
            Q118=makeQuery(id+"F2.imprint","IMPRINT",FACE,{"disambiguationData":[TD([[makeQuery(id+"F2.imprint","IMPRINT",EDGE,{"derivedFrom":sQuery(id+"F2.wireOp",EDGE,"E2.0.1.0")}),1.0]])]});
            var Q119;
            Q119=makeQuery(id+"F2.imprint","IMPRINT",FACE,{"disambiguationData":[TD([[makeQuery(id+"F2.imprint","IMPRINT",EDGE,{"derivedFrom":sQuery(id+"F2.wireOp",EDGE,"E1")}),1.0]])]});
            extrude(context, id + "F3", {"entities" : qUnion([Q0, Q1, Q2, Q3, Q4, Q5, Q6, Q7, Q8, Q9, Q10, Q11, Q12, Q13, Q14, Q15, Q16, Q17, Q18, Q19, Q20, Q21, Q22, Q23, Q24, Q25, Q26, Q27, Q28, Q29, Q30, Q31, Q32, Q33, Q34, Q35, Q36, Q37, Q38, Q39, Q40, Q41, Q42, Q43, Q44, Q45, Q46, Q47, Q48, Q49, Q50, Q51, Q52, Q53, Q54, Q55, Q56, Q57, Q58, Q59, Q60, Q61, Q62, Q63, Q64, Q65, Q66, Q67, Q68, Q69, Q70, Q71, Q72, Q73, Q74, Q75, Q76, Q77, Q78, Q79, Q80, Q81, Q82, Q83, Q84, Q85, Q86, Q87, Q88, Q89, Q90, Q91, Q92, Q93, Q94, Q95, Q96, Q97, Q98, Q99, Q100, Q101, Q102, Q103, Q104, Q105, Q106, Q107, Q108, Q109, Q110, Q111, Q112, Q113, Q114, Q115, Q116, Q117, Q118, Q119]), "operationType" : NewBodyOperationType.REMOVE, "oppositeDirection" : true, "depth" : 25.4 * mm});
        }
    });
